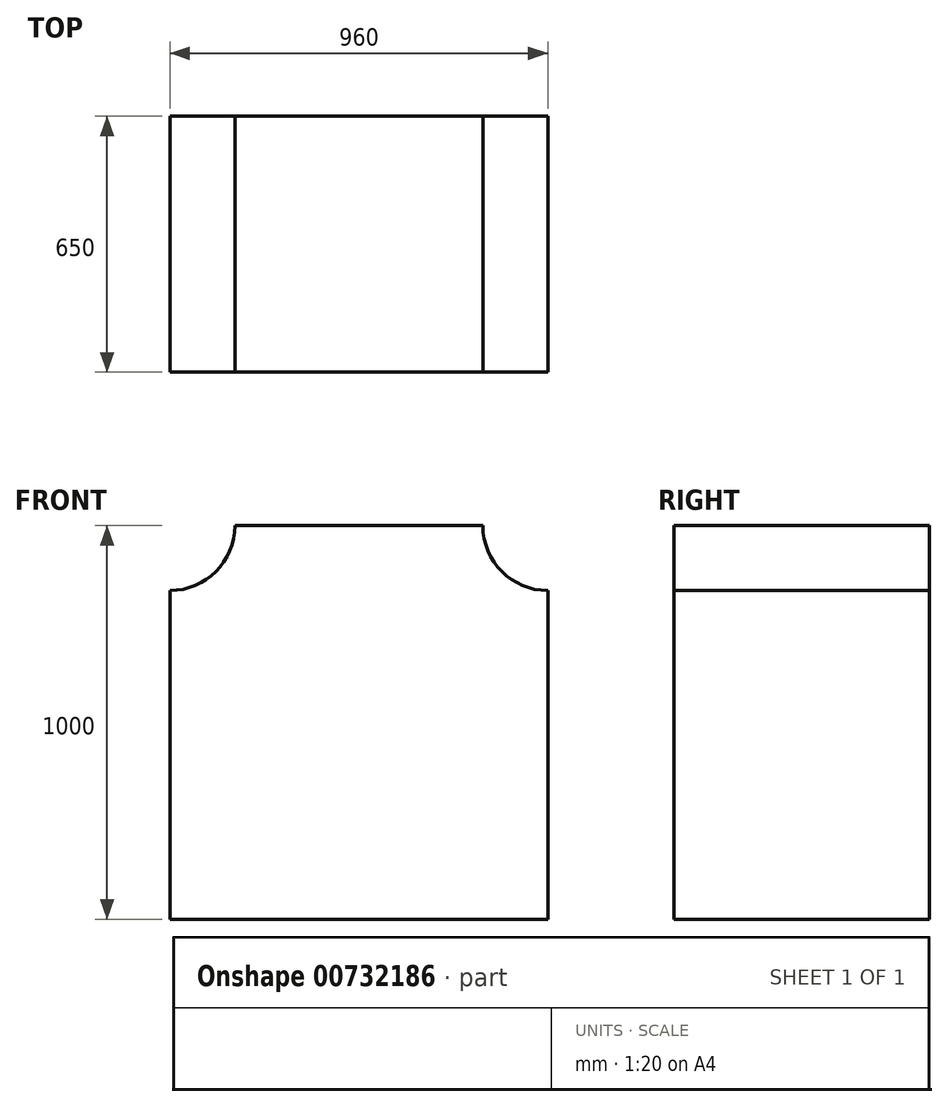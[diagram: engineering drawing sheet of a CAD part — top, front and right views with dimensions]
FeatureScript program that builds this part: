
annotation { "Feature Type Name" : "Feature", "Feature Type Description" : "" }
export const myFeature = defineFeature(function(context is Context, id is Id, definition is map)
    precondition{}
    {
        {
            var Q0;
            Q0=qCreatedBy(makeId("Front.planeOp"),FACE);
            var sketch = newSketch(context, id + "F0", { "sketchPlane" : qUnion([Q0])});
            skLineSegment(sketch, "E0.left", {"start": v(-802.53, 0) * mm, "end": v(-802.53, 0) * mm});
            skLineSegment(sketch, "E0.right", {"start": v(1024.88, 0) * mm, "end": v(1024.88, 0) * mm});
            skLineSegment(sketch, "E1.bottom", {"start": v(-480, 0) * mm, "end": v(480, 0) * mm});
            skLineSegment(sketch, "E1.top", {"start": v(-315, 1000) * mm, "end": v(315, 1000) * mm});
            skLineSegment(sketch, "E1.left", {"start": v(-480, 0) * mm, "end": v(-480, 835) * mm});
            skLineSegment(sketch, "E1.right", {"start": v(480, 0) * mm, "end": v(480, 835) * mm});
            skPoint(sketch, "E2", {"position": v(0, 1000) * mm});
            skArc(sketch, "E3", {"start": v(315, 1000) * mm, "mid": v(363.33, 883.33) * mm, "end": v(480, 835) * mm});
            skLineSegment(sketch, "E4", {"start": v(0, 1000) * mm, "end": v(0, 0) * mm, "construction": true});
            skArc(sketch, "E5.MirrorC", {"start": v(-315, 1000) * mm, "mid": v(-363.33, 883.33) * mm, "end": v(-480, 835) * mm});
            skSolve(sketch);
        }
        {
            var Q0;
            Q0 = qSketchRegion(id + "F0", true);
            extrude(context, id + "F1", {"entities" : qUnion([Q0]), "endBound" : BoundingType.SYMMETRIC, "depth" : 650 * mm, "offsetDistance" : 25 * mm});
        }
    });
